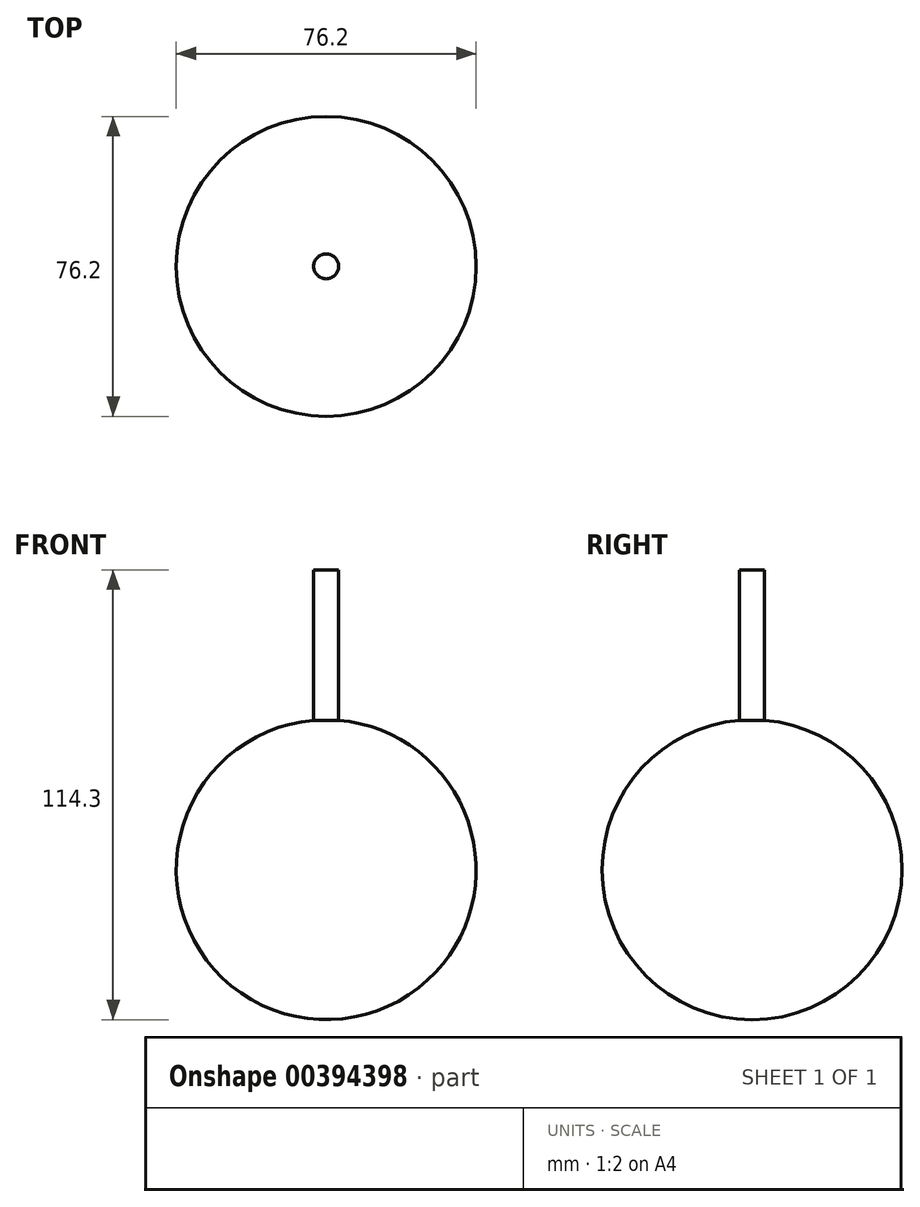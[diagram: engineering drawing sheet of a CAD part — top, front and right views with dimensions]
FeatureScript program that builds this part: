
annotation { "Feature Type Name" : "Feature", "Feature Type Description" : "" }
export const myFeature = defineFeature(function(context is Context, id is Id, definition is map)
    precondition{}
    {
        {
            var Q0;
            Q0=qCreatedBy(makeId("Top.planeOp"),FACE);
            var sketch = newSketch(context, id + "F0", { "sketchPlane" : qUnion([Q0])});
            skCircle(sketch, "E0", {"center": v(0, 0) * mm, "radius": 38.1 * mm});
            skLineSegment(sketch, "E1", {"start": v(0, 0) * mm, "end": v(0, 38.1) * mm});
            skLineSegment(sketch, "E2", {"start": v(0, 0) * mm, "end": v(0, -38.1) * mm});
            skCircle(sketch, "E3", {"center": v(0, 0) * mm, "radius": 3.18 * mm});
            skSolve(sketch);
        }
        {
            var Q0;
            {var subQ0=sQuery(id+"F0.wireOp",EDGE,"E1");Q0=makeQuery(id+"F0.imprint","IMPRINT",FACE,{"disambiguationData":[TD([[makeQuery(id+"F0.imprint","IMPRINT",EDGE,{"derivedFrom":subQ0}),-1.0]])]});}
            var Q1;
            {var subQ0=sQuery(id+"F0.wireOp",EDGE,"E1");var subQ1=sQuery(id+"F0.wireOp",EDGE,"E0");var subQ2=makeQuery(id+"F0.imprint","INTERSECT",VERTEX,{"derivedFrom":[subQ1,subQ0]});Q1=makeQuery(id+"F0.imprint","IMPRINT",FACE,{"disambiguationData":[TD([[makeQuery(id+"F0.imprint","IMPRINT",EDGE,{"disambiguationData":[TD([[subQ2,1.0]])],"derivedFrom":subQ1}),1.0]])]});}
            var Q2;
            Q2=sQuery(id+"F0.wireOp",EDGE,"E2");
            revolve(context, id + "F1", {"entities" : qUnion([Q0, Q1]), "axis" : qUnion([Q2]), "revolveType" : RevolveType.FULL});
        }
        {
            var Q0;
            {var subQ0=sQuery(id+"F0.wireOp",EDGE,"E2");var subQ1=sQuery(id+"F0.wireOp",EDGE,"E1");var subQ2=makeQuery(id+"F0.imprint","INTERSECT",VERTEX,{"derivedFrom":[subQ1,subQ0]});Q0=makeQuery(id+"F0.imprint","IMPRINT",FACE,{"disambiguationData":[TD([[makeQuery(id+"F0.imprint","IMPRINT",EDGE,{"disambiguationData":[TD([[subQ2,-1.0]])],"derivedFrom":subQ1}),1.0]])]});}
            var Q1;
            {var subQ0=sQuery(id+"F0.wireOp",EDGE,"E2");var subQ1=sQuery(id+"F0.wireOp",EDGE,"E1");var subQ2=makeQuery(id+"F0.imprint","INTERSECT",VERTEX,{"derivedFrom":[subQ1,subQ0]});Q1=makeQuery(id+"F0.imprint","IMPRINT",FACE,{"disambiguationData":[TD([[makeQuery(id+"F0.imprint","IMPRINT",EDGE,{"disambiguationData":[TD([[subQ2,-1.0]])],"derivedFrom":subQ1}),-1.0]])]});}
            extrude(context, id + "F2", {"entities" : qUnion([Q0, Q1]), "operationType" : NewBodyOperationType.ADD, "depth" : 76.2 * mm});
        }
    });
